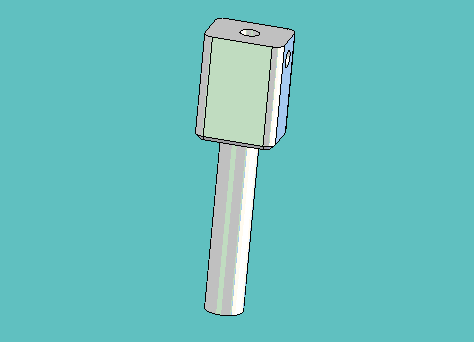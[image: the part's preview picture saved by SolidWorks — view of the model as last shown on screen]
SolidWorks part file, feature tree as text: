
SOLIDWORKS PART (.sldprt)
format: sldprt  version: not decoded by parser v0  size: 486,400 bytes
history: native  units: mm
features: sketch x5, cut_extrude x2, material x1, revolve x1, extrude x1, fillet x1, chamfer x1 (+11 scaffold rows collapsed)
feature tree (23):
  scaffold x11  (default folders/planes/origin — collapsed)
  material  "Material <not specified>"
  sketch  "Sketch1"  dims[D1=~23.41245mm D2=9.525mm D3=6.0452mm D4=~45.24375mm]
  revolve  "Revolve1"  Angle=360deg
  sketch  "Sketch5"  dims[D3=12.7mm D1=4.7625mm D2=4.7625mm]
  extrude  "Extrude1"  [1 undecoded]
  sketch  "Sketch3"  dims[D1=3.048mm]
  cut_extrude  "Cut-Extrude2"  Depth=9.525mm
  sketch  "Sketch4"  dims[D2=2.7051mm D1=3.175mm]
  cut_extrude  "Cut-Extrude3"  [1 undecoded]
  sketch  "Sketch2"  dims[D1=~5.58546mm]
  fillet  "Fillet1"  Radius=1.5875mm
  chamfer  "Chamfer1"  Distance=0.762mm Angle=45deg
decode coverage: 9 of 11 modeling features carry decoded parameters
note: ~ marks probable driven/reference dimensions
note: 2 parameter values undecoded
note: suppression state not decoded; provenance and decode notes live in map.json
